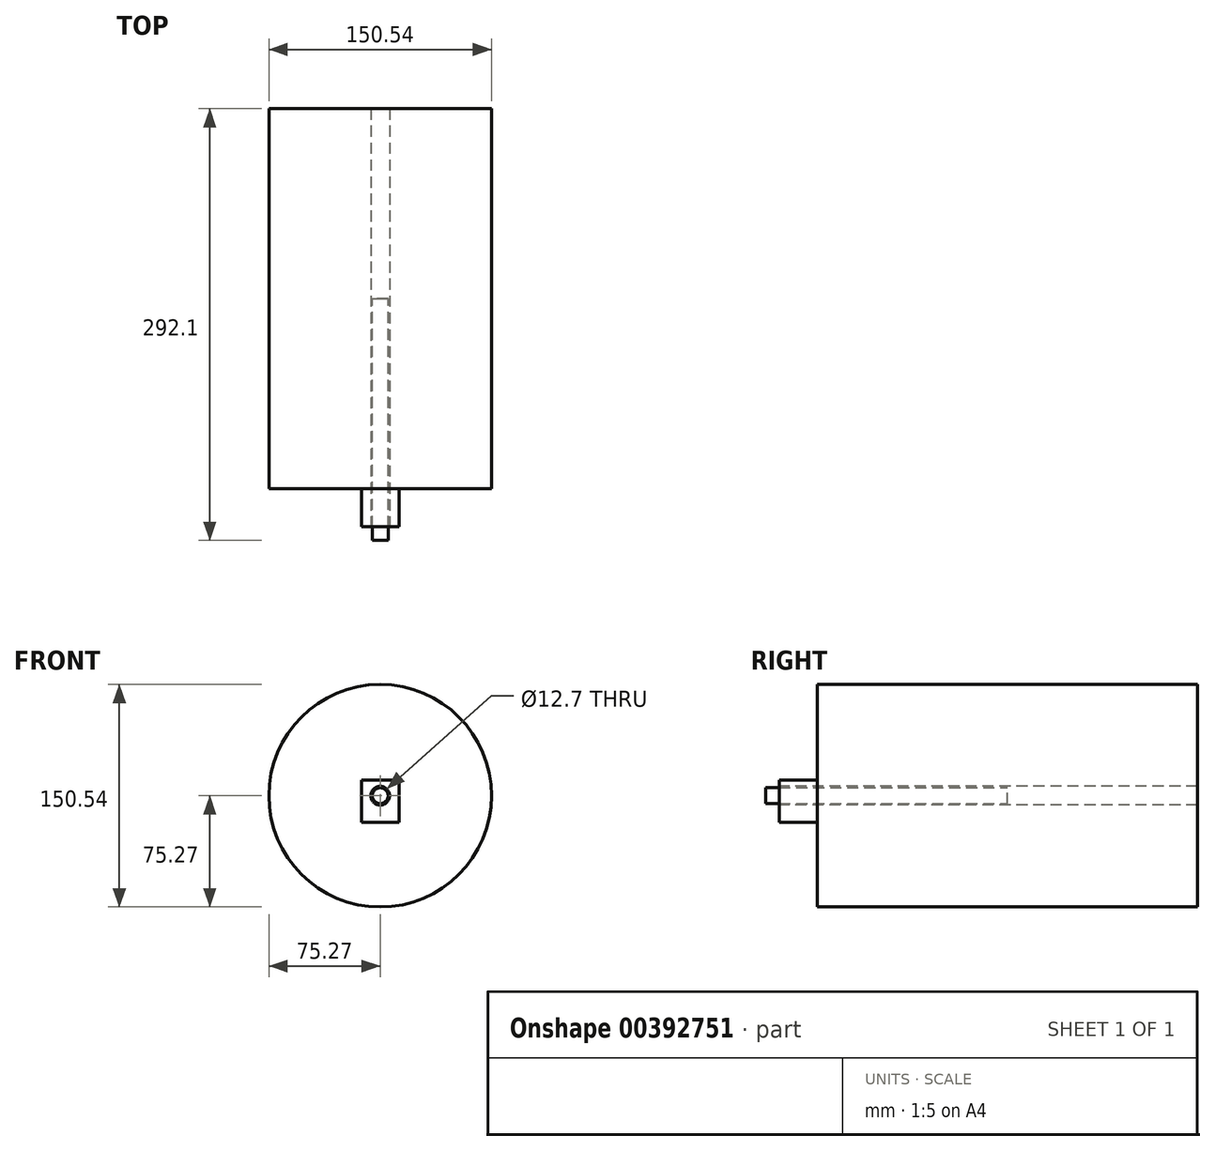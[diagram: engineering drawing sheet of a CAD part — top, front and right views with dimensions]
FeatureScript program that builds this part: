
annotation { "Feature Type Name" : "Feature", "Feature Type Description" : "" }
export const myFeature = defineFeature(function(context is Context, id is Id, definition is map)
    precondition{}
    {
        {
            var Q0;
            Q0=qCreatedBy(makeId("Front.planeOp"),FACE);
            var sketch = newSketch(context, id + "F0", { "sketchPlane" : qUnion([Q0])});
            skCircle(sketch, "E0", {"center": v(0, 0) * mm, "radius": 75.27 * mm});
            skSolve(sketch);
        }
        {
            var Q0;
            Q0=makeQuery(id+"F0.imprint","IMPRINT",FACE,{"disambiguationData":[TD([[makeQuery(id+"F0.imprint","IMPRINT",EDGE,{"derivedFrom":sQuery(id+"F0.wireOp",EDGE,"E0")}),1.0]])]});
            extrude(context, id + "F1", {"entities" : qUnion([Q0]), "endBound" : BoundingType.SYMMETRIC, "depth" : 257.05 * mm});
        }
        {
            var Q0;
            Q0=qCreatedBy(makeId("Front.planeOp"),FACE);
            var sketch = newSketch(context, id + "F2", { "sketchPlane" : qUnion([Q0])});
            skLineSegment(sketch, "E1.bottom", {"start": v(-12.71, -17.85) * mm, "end": v(12.71, -17.85) * mm});
            skLineSegment(sketch, "E1.top", {"start": v(-12.71, 10.51) * mm, "end": v(12.71, 10.51) * mm});
            skLineSegment(sketch, "E1.left", {"start": v(-12.71, -17.85) * mm, "end": v(-12.71, 10.51) * mm});
            skLineSegment(sketch, "E1.right", {"start": v(12.71, -17.85) * mm, "end": v(12.71, 10.51) * mm});
            skPoint(sketch, "E1.middle", {"position": v(0, -3.67) * mm});
            skSolve(sketch);
        }
        {
            var Q0;
            Q0 = qSketchRegion(id + "F2", true);
            extrude(context, id + "F3", {"entities" : qUnion([Q0]), "operationType" : NewBodyOperationType.ADD, "depth" : 154.43 * mm});
        }
        {
            var Q0;
            Q0=makeQuery(id+"F3.opExtrude","CAP_FACE",FACE,{"disambiguationData":[OSD([sQuery(id+"F2.wireOp",EDGE,"E1.bottom"),sQuery(id+"F2.wireOp",EDGE,"E1.top"),sQuery(id+"F2.wireOp",EDGE,"E1.left"),sQuery(id+"F2.wireOp",EDGE,"E1.right")])],"isStart":false});
            var sketch = newSketch(context, id + "F4", { "sketchPlane" : qUnion([Q0])});
            skCircle(sketch, "E2", {"center": v(0, 0) * mm, "radius": 7.88 * mm});
            skSolve(sketch);
        }
        {
            var Q0;
            Q0=sQuery(id+"F4.wireOp",VERTEX,"E2.center");
            var Q1;
            Q1=makeQuery(id+"F1.opExtrude","SWEPT_BODY",BODY,{"disambiguationData":[OSD([sQuery(id+"F0.wireOp",EDGE,"E0")])]});
            hole(context, id + "F5", {"style" : HoleStyle.SIMPLE, "endStyle" : HoleEndStyle.THROUGH, "holeDiameter" : 12.7 * mm, "isTappedThrough" : true, "tappedDepth" : 12.7 * mm, "tapClearance" : 3, "locations" : qUnion([Q0]), "scope" : qUnion([Q1])});
        }
        {
            var Q0;
            Q0=qCreatedBy(makeId("Front.planeOp"),FACE);
            var sketch = newSketch(context, id + "F6", { "sketchPlane" : qUnion([Q0])});
            skCircle(sketch, "E3", {"center": v(0, 0) * mm, "radius": 5.36 * mm});
            skSolve(sketch);
        }
        {
            var Q0;
            Q0 = qSketchRegion(id + "F6", true);
            extrude(context, id + "F7", {"entities" : qUnion([Q0]), "depth" : 163.58 * mm});
        }
    });
